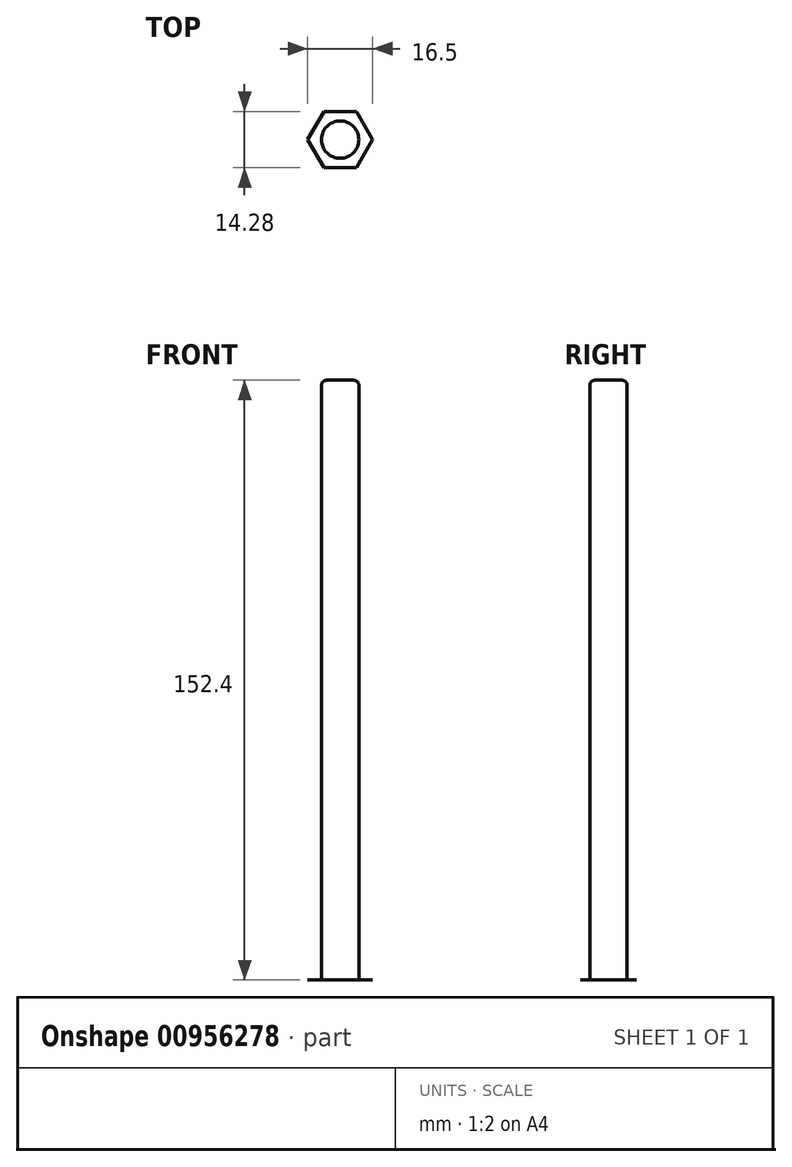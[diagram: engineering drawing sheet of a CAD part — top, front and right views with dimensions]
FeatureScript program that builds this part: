
annotation { "Feature Type Name" : "Feature", "Feature Type Description" : "" }
export const myFeature = defineFeature(function(context is Context, id is Id, definition is map)
    precondition{}
    {
        {
            var Q0;
            Q0=qCreatedBy(makeId("Top.planeOp"),FACE);
            var sketch = newSketch(context, id + "F0", { "sketchPlane" : qUnion([Q0])});
            skCircle(sketch, "E0", {"center": v(0, 0) * mm, "radius": 4.75 * mm});
            skSolve(sketch);
        }
        {
            var Q0;
            Q0=qSketchRegion(id+"F0",true);
            extrude(context, id + "F1", {"entities" : qUnion([Q0]), "depth" : 152.4 * mm, "offsetDistance" : 25.4 * mm});
        }
        {
            var Q0;
            Q0=qCreatedBy(makeId("Top.planeOp"),FACE);
            var sketch = newSketch(context, id + "F2", { "sketchPlane" : qUnion([Q0])});
            skCircle(sketch, "E1.cCircle", {"center": v(0, 0) * mm, "radius": 7.14 * mm, "construction": true});
            skLineSegment(sketch, "E1.0", {"start": v(4.12, -7.14) * mm, "end": v(-4.12, -7.14) * mm});
            skLineSegment(sketch, "E1.1", {"start": v(-4.12, -7.14) * mm, "end": v(-8.25, 0) * mm});
            skLineSegment(sketch, "E1.2", {"start": v(-8.25, 0) * mm, "end": v(-4.12, 7.14) * mm});
            skLineSegment(sketch, "E1.3", {"start": v(-4.12, 7.14) * mm, "end": v(4.12, 7.14) * mm});
            skLineSegment(sketch, "E1.4", {"start": v(4.12, 7.14) * mm, "end": v(8.25, 0) * mm});
            skLineSegment(sketch, "E1.5", {"start": v(8.25, 0) * mm, "end": v(4.12, -7.14) * mm});
            skPoint(sketch, "E1.0.midPoint", {"position": v(0, -7.14) * mm});
            skSolve(sketch);
        }
        {
            var Q0;
            Q0=qSketchRegion(id+"F2",true);
            extrude(context, id + "F3", {"entities" : qUnion([Q0]), "operationType" : NewBodyOperationType.ADD, "depth" : 21 / 1625.6 * mm, "offsetDistance" : 25.4 * mm});
        }
        {
            var Q0;
            Q0=makeQuery(id+"F1.opExtrude","CAP_EDGE",EDGE,{"disambiguationData":[OSD([sQuery(id+"F0.wireOp",EDGE,"E0")])],"isStart":false});
            fillet(context, id + "F4", {"entities" : qUnion([Q0]), "radius" : 1.27 * mm, "tangentPropagation" : true, "allowEdgeOverflow" : false});
        }
    });
